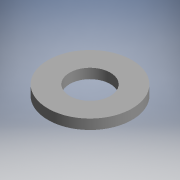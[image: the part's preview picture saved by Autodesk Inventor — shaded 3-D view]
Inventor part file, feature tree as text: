
AUTODESK INVENTOR PART (.ipt)
format: ipt  version: 2017.3 (Build 213256000, 256)  size: 90,624 bytes
history: native  units: mm (DEFAULTED — no unit token found)
features: other x7, extrude x1, sketch x1
ambient origin geometry x8: Origin, YZ Plane, XZ Plane, XY Plane, X Axis, Y Axis, Z Axis, Center Point
bodies: Solid1 (feature_tree)
feature tree (9):
  extrude  "Extrusion1"  TaperAngle=0.0deg  [1 undecoded]
  other  "washer_to_bolt_XY"
  other  "washer_to_bolt_YZ"
  other  "washer_to_bolt_ZX"
  other  "washer_to_bolt_X"
  other  "washer_to_bolt_Y"
  other  "washer_to_bolt_Z"
  other  "washer_to_bolt_Center"
  sketch  "Sketch_2"  dims[d0=2.0mm d1=0.0mm d2=0.0mm]
note: 1 required parameter value undecoded (feature->parameter linkage not recoverable at this tier; creation-order binding heuristic only, values carry confidence <= 0.55)
